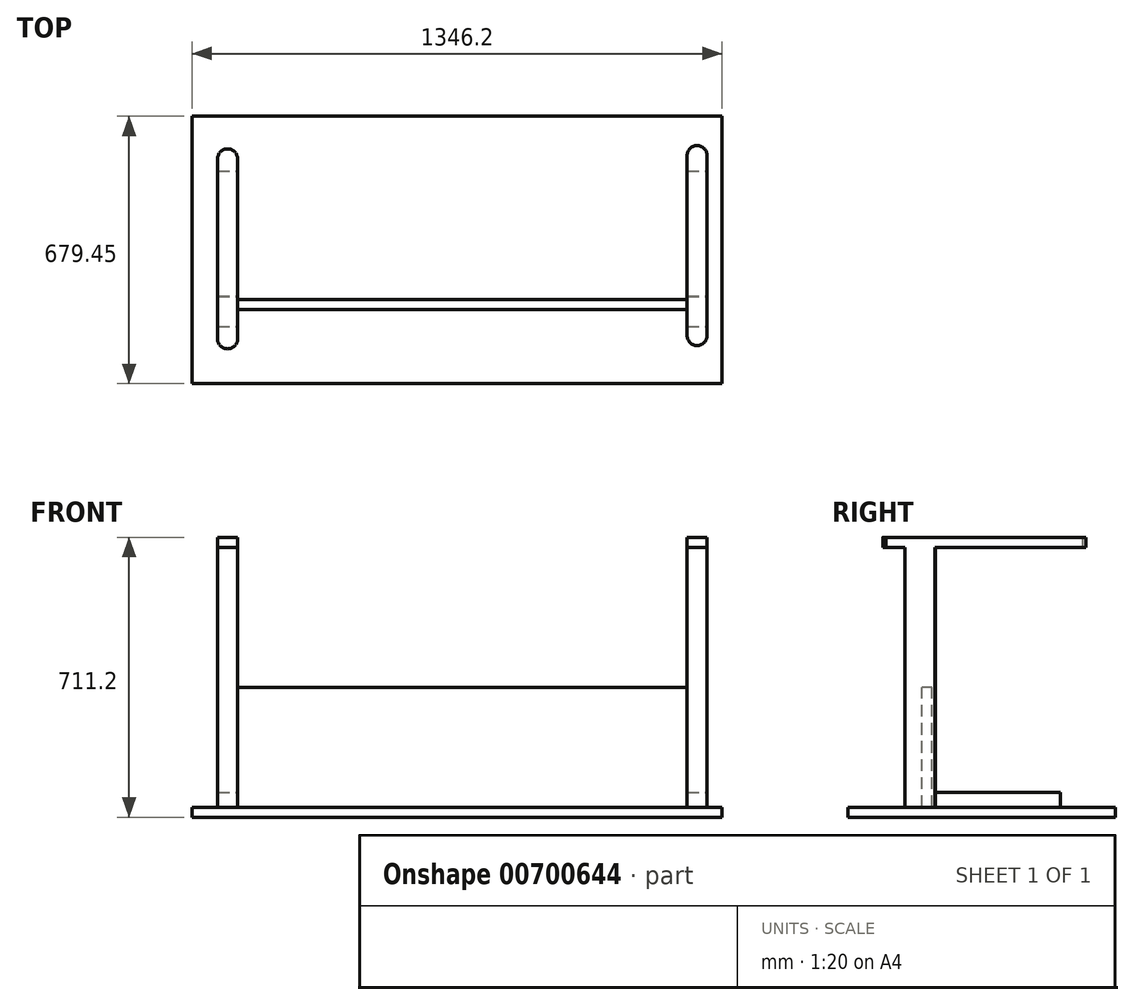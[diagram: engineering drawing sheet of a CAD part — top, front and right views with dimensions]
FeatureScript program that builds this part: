
annotation { "Feature Type Name" : "Feature", "Feature Type Description" : "" }
export const myFeature = defineFeature(function(context is Context, id is Id, definition is map)
    precondition{}
    {
        {
            var Q0;
            Q0=qCreatedBy(makeId("Top.planeOp"),FACE);
            var sketch = newSketch(context, id + "F0", { "sketchPlane" : qUnion([Q0])});
            skLineSegment(sketch, "E0.bottom", {"start": v(-524.08, 343.16) * mm, "end": v(822.12, 343.16) * mm});
            skLineSegment(sketch, "E0.top", {"start": v(-524.08, -336.3) * mm, "end": v(822.12, -336.3) * mm});
            skLineSegment(sketch, "E0.left", {"start": v(-524.08, 343.16) * mm, "end": v(-524.08, -336.3) * mm});
            skLineSegment(sketch, "E0.right", {"start": v(822.12, 343.16) * mm, "end": v(822.12, -336.3) * mm});
            skSolve(sketch);
        }
        {
            var Q0;
            Q0 = qSketchRegion(id + "F0", true);
            extrude(context, id + "F1", {"entities" : qUnion([Q0]), "depth" : 25.4 * mm, "offsetDistance" : 25.4 * mm});
        }
        {
            var Q0;
            Q0=makeQuery(id+"F1.opExtrude","CAP_FACE",FACE,{"disambiguationData":[OSD([sQuery(id+"F0.wireOp",EDGE,"E0.bottom"),sQuery(id+"F0.wireOp",EDGE,"E0.top"),sQuery(id+"F0.wireOp",EDGE,"E0.left"),sQuery(id+"F0.wireOp",EDGE,"E0.right")])],"isStart":false});
            var sketch = newSketch(context, id + "F2", { "sketchPlane" : qUnion([Q0])});
            skSolve(sketch);
        }
        {
            var Q0;
            Q0=makeQuery(id+"F1.opExtrude","CAP_FACE",FACE,{"disambiguationData":[OSD([sQuery(id+"F0.wireOp",EDGE,"E0.bottom"),sQuery(id+"F0.wireOp",EDGE,"E0.top"),sQuery(id+"F0.wireOp",EDGE,"E0.left"),sQuery(id+"F0.wireOp",EDGE,"E0.right")])],"isStart":false});
            var sketch = newSketch(context, id + "F3", { "sketchPlane" : qUnion([Q0])});
            skLineSegment(sketch, "E1.bottom", {"start": v(-458.93, 203.46) * mm, "end": v(-408.13, 203.46) * mm});
            skLineSegment(sketch, "E1.top", {"start": v(-458.93, -114.04) * mm, "end": v(-408.13, -114.04) * mm});
            skLineSegment(sketch, "E1.left", {"start": v(-458.93, 203.46) * mm, "end": v(-458.93, -114.04) * mm});
            skLineSegment(sketch, "E1.right", {"start": v(-408.13, 203.46) * mm, "end": v(-408.13, -114.04) * mm});
            skSolve(sketch);
        }
        {
            var Q0;
            Q0=makeQuery(id+"F2.imprint","IMPRINT",FACE,{"disambiguationData":[TD([[makeQuery(id+"F2.imprint","IMPRINT",EDGE,{"derivedFrom":makeQuery(id+"F1.opExtrude","CAP_EDGE",EDGE,{"disambiguationData":[OSD([sQuery(id+"F0.wireOp",EDGE,"E0.bottom")])],"isStart":false})}),-1.0]])]});
            var sketch = newSketch(context, id + "F4", { "sketchPlane" : qUnion([Q0])});
            skLineSegment(sketch, "E2.bottom", {"start": v(733.49, 203.46) * mm, "end": v(784.29, 203.46) * mm});
            skLineSegment(sketch, "E2.top", {"start": v(733.49, -114.04) * mm, "end": v(784.29, -114.04) * mm});
            skLineSegment(sketch, "E2.left", {"start": v(733.49, 203.46) * mm, "end": v(733.49, -114.04) * mm});
            skLineSegment(sketch, "E2.right", {"start": v(784.29, 203.46) * mm, "end": v(784.29, -114.04) * mm});
            skSolve(sketch);
        }
        {
            var Q0;
            Q0=makeQuery(id+"F3.imprint","IMPRINT",FACE,{"disambiguationData":[TD([[makeQuery(id+"F3.imprint","IMPRINT",EDGE,{"derivedFrom":sQuery(id+"F3.wireOp",EDGE,"E1.bottom")}),-1.0]])]});
            var Q1;
            Q1=makeQuery(id+"F4.imprint","IMPRINT",FACE,{"disambiguationData":[TD([[makeQuery(id+"F4.imprint","IMPRINT",EDGE,{"derivedFrom":sQuery(id+"F4.wireOp",EDGE,"E2.bottom")}),-1.0]])]});
            extrude(context, id + "F5", {"entities" : qUnion([Q0, Q1]), "operationType" : NewBodyOperationType.ADD, "depth" : 38.1 * mm, "offsetDistance" : 25.4 * mm});
        }
        {
            var Q0;
            Q0=makeQuery(id+"F2.imprint","IMPRINT",FACE,{"disambiguationData":[TD([[makeQuery(id+"F2.imprint","IMPRINT",EDGE,{"derivedFrom":makeQuery(id+"F1.opExtrude","CAP_EDGE",EDGE,{"disambiguationData":[OSD([sQuery(id+"F0.wireOp",EDGE,"E0.bottom")])],"isStart":false})}),-1.0]])]});
            var sketch = newSketch(context, id + "F6", { "sketchPlane" : qUnion([Q0])});
            skLineSegment(sketch, "E3.bottom", {"start": v(733.52, -114.86) * mm, "end": v(784.32, -114.86) * mm});
            skLineSegment(sketch, "E3.top", {"start": v(733.52, -191.06) * mm, "end": v(784.32, -191.06) * mm});
            skLineSegment(sketch, "E3.left", {"start": v(733.52, -114.86) * mm, "end": v(733.52, -191.06) * mm});
            skLineSegment(sketch, "E3.right", {"start": v(784.32, -114.86) * mm, "end": v(784.32, -191.06) * mm});
            skSolve(sketch);
        }
        {
            var Q0;
            Q0=makeQuery(id+"F2.imprint","IMPRINT",FACE,{"disambiguationData":[TD([[makeQuery(id+"F2.imprint","IMPRINT",EDGE,{"derivedFrom":makeQuery(id+"F1.opExtrude","CAP_EDGE",EDGE,{"disambiguationData":[OSD([sQuery(id+"F0.wireOp",EDGE,"E0.bottom")])],"isStart":false})}),-1.0]])]});
            var sketch = newSketch(context, id + "F7", { "sketchPlane" : qUnion([Q0])});
            skLineSegment(sketch, "E4.bottom", {"start": v(-459.36, -114.18) * mm, "end": v(-408.56, -114.18) * mm});
            skLineSegment(sketch, "E4.top", {"start": v(-459.36, -190.38) * mm, "end": v(-408.56, -190.38) * mm});
            skLineSegment(sketch, "E4.left", {"start": v(-459.36, -114.18) * mm, "end": v(-459.36, -190.38) * mm});
            skLineSegment(sketch, "E4.right", {"start": v(-408.56, -114.18) * mm, "end": v(-408.56, -190.38) * mm});
            skSolve(sketch);
        }
        {
            var Q0;
            Q0 = qSketchRegion(id + "F7", true);
            var Q1;
            Q1 = qSketchRegion(id + "F6", true);
            extrude(context, id + "F8", {"entities" : qUnion([Q0, Q1]), "operationType" : NewBodyOperationType.ADD, "depth" : 660.4 * mm, "offsetDistance" : 25.4 * mm});
        }
        {
            var Q0;
            Q0=makeQuery(id+"F8.opExtrude","CAP_FACE",FACE,{"disambiguationData":[OSD([sQuery(id+"F7.wireOp",EDGE,"E4.bottom"),sQuery(id+"F7.wireOp",EDGE,"E4.top"),sQuery(id+"F7.wireOp",EDGE,"E4.left"),sQuery(id+"F7.wireOp",EDGE,"E4.right")])],"isStart":false});
            var sketch = newSketch(context, id + "F9", { "sketchPlane" : qUnion([Q0])});
            skPoint(sketch, "E5.oppositeSnap0", {"position": v(-408.56, -152.28) * mm});
            skLineSegment(sketch, "E5.bottom", {"start": v(-459.36, -247.5) * mm, "end": v(-408.56, -247.5) * mm});
            skLineSegment(sketch, "E5.top", {"start": v(-459.36, 260.5) * mm, "end": v(-408.56, 260.5) * mm});
            skLineSegment(sketch, "E5.left", {"start": v(-459.36, -247.5) * mm, "end": v(-459.36, 260.5) * mm});
            skLineSegment(sketch, "E5.right", {"start": v(-408.56, -247.5) * mm, "end": v(-408.56, 260.5) * mm});
            skSolve(sketch);
        }
        {
            var Q0;
            Q0=makeQuery(id+"F8.opExtrude","CAP_FACE",FACE,{"disambiguationData":[OSD([sQuery(id+"F6.wireOp",EDGE,"E3.bottom"),sQuery(id+"F6.wireOp",EDGE,"E3.top"),sQuery(id+"F6.wireOp",EDGE,"E3.left"),sQuery(id+"F6.wireOp",EDGE,"E3.right")])],"isStart":false});
            var sketch = newSketch(context, id + "F10", { "sketchPlane" : qUnion([Q0])});
            skLineSegment(sketch, "E6.bottom", {"start": v(733.52, -239.09) * mm, "end": v(784.32, -239.09) * mm});
            skLineSegment(sketch, "E6.top", {"start": v(733.52, 268.91) * mm, "end": v(784.32, 268.91) * mm});
            skLineSegment(sketch, "E6.left", {"start": v(733.52, -239.09) * mm, "end": v(733.52, 268.91) * mm});
            skLineSegment(sketch, "E6.right", {"start": v(784.32, -239.09) * mm, "end": v(784.32, 268.91) * mm});
            skSolve(sketch);
        }
        {
            var Q0;
            Q0 = qSketchRegion(id + "F10", true);
            var Q1;
            Q1 = qSketchRegion(id + "F9", true);
            extrude(context, id + "F11", {"entities" : qUnion([Q0, Q1]), "operationType" : NewBodyOperationType.ADD, "depth" : 25.4 * mm, "offsetDistance" : 25.4 * mm});
        }
        {
            var Q0;
            Q0=makeQuery(id+"F11.opExtrude","SWEPT_EDGE",EDGE,{"disambiguationData":[OSD([sQuery(id+"F9.wireOp",EDGE,"E5.top"),sQuery(id+"F9.wireOp",EDGE,"E5.left")])]});
            var Q1;
            Q1=makeQuery(id+"F11.opExtrude","SWEPT_EDGE",EDGE,{"disambiguationData":[OSD([sQuery(id+"F9.wireOp",EDGE,"E5.top"),sQuery(id+"F9.wireOp",EDGE,"E5.right")])]});
            var Q2;
            Q2=makeQuery(id+"F11.opExtrude","SWEPT_EDGE",EDGE,{"disambiguationData":[OSD([sQuery(id+"F10.wireOp",EDGE,"E6.top"),sQuery(id+"F10.wireOp",EDGE,"E6.left")])]});
            var Q3;
            Q3=makeQuery(id+"F11.opExtrude","SWEPT_EDGE",EDGE,{"disambiguationData":[OSD([sQuery(id+"F10.wireOp",EDGE,"E6.top"),sQuery(id+"F10.wireOp",EDGE,"E6.right")])]});
            var Q4;
            Q4=makeQuery(id+"F11.opExtrude","SWEPT_EDGE",EDGE,{"disambiguationData":[OSD([sQuery(id+"F9.wireOp",EDGE,"E5.bottom"),sQuery(id+"F9.wireOp",EDGE,"E5.left")])]});
            var Q5;
            Q5=makeQuery(id+"F11.opExtrude","SWEPT_EDGE",EDGE,{"disambiguationData":[OSD([sQuery(id+"F9.wireOp",EDGE,"E5.bottom"),sQuery(id+"F9.wireOp",EDGE,"E5.right")])]});
            var Q6;
            Q6=makeQuery(id+"F11.opExtrude","SWEPT_EDGE",EDGE,{"disambiguationData":[OSD([sQuery(id+"F10.wireOp",EDGE,"E6.bottom"),sQuery(id+"F10.wireOp",EDGE,"E6.left")])]});
            fillet(context, id + "F12", {"entities" : qUnion([Q0, Q1, Q2, Q3, Q4, Q5, Q6]), "radius" : 25.4 * mm, "tangentPropagation" : true, "allowEdgeOverflow" : false});
        }
        {
            var Q0;
            Q0=makeQuery(id+"F11.opExtrude","SWEPT_EDGE",EDGE,{"disambiguationData":[OSD([sQuery(id+"F10.wireOp",EDGE,"E6.bottom"),sQuery(id+"F10.wireOp",EDGE,"E6.right")])]});
            fillet(context, id + "F13", {"entities" : qUnion([Q0]), "radius" : 25.4 * mm, "tangentPropagation" : true, "allowEdgeOverflow" : false});
        }
        {
            var Q0;
            Q0=makeQuery(id+"F2.imprint","IMPRINT",FACE,{"disambiguationData":[TD([[makeQuery(id+"F2.imprint","IMPRINT",EDGE,{"derivedFrom":makeQuery(id+"F1.opExtrude","CAP_EDGE",EDGE,{"disambiguationData":[OSD([sQuery(id+"F0.wireOp",EDGE,"E0.bottom")])],"isStart":false})}),-1.0]])]});
            var sketch = newSketch(context, id + "F14", { "sketchPlane" : qUnion([Q0])});
            skLineSegment(sketch, "E7.bottom", {"start": v(-408.36, -147.74) * mm, "end": v(735, -147.74) * mm});
            skLineSegment(sketch, "E7.top", {"start": v(-408.36, -122.34) * mm, "end": v(735, -122.34) * mm});
            skLineSegment(sketch, "E7.left", {"start": v(-408.36, -147.74) * mm, "end": v(-408.36, -122.34) * mm});
            skLineSegment(sketch, "E7.right", {"start": v(735, -147.74) * mm, "end": v(735, -122.34) * mm});
            skSolve(sketch);
        }
        {
            var Q0;
            Q0 = qSketchRegion(id + "F14", true);
            extrude(context, id + "F15", {"entities" : qUnion([Q0]), "operationType" : NewBodyOperationType.ADD, "depth" : 304.8 * mm, "offsetDistance" : 25.4 * mm});
        }
    });
